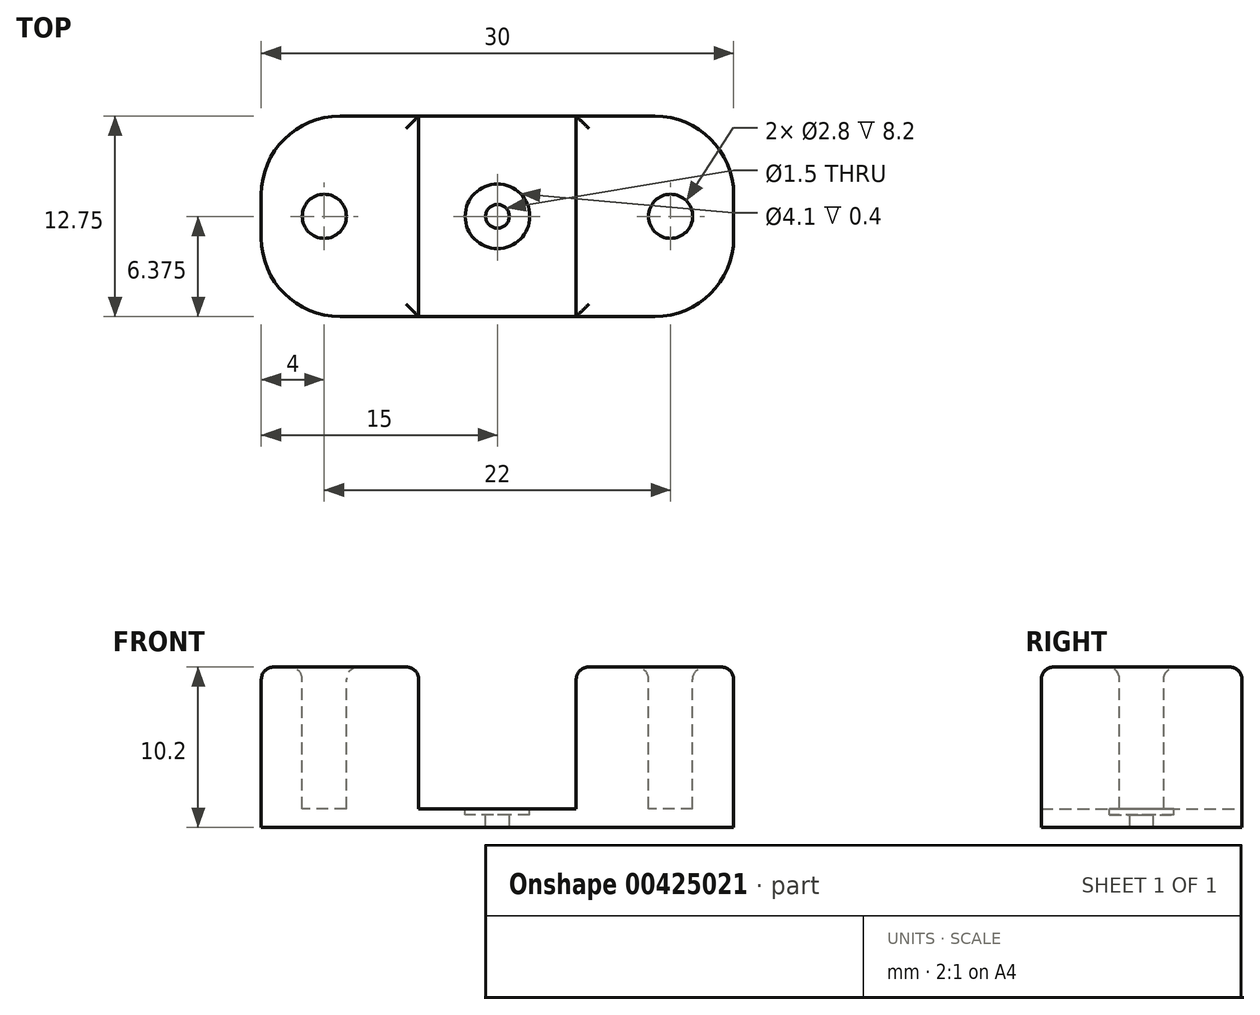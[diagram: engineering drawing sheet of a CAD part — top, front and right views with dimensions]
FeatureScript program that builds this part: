
annotation { "Feature Type Name" : "Feature", "Feature Type Description" : "" }
export const myFeature = defineFeature(function(context is Context, id is Id, definition is map)
    precondition{}
    {
        {
            var Q0;
            Q0=qCreatedBy(makeId("Front.planeOp"),FACE);
            var sketch = newSketch(context, id + "F0", { "sketchPlane" : qUnion([Q0])});
            skLineSegment(sketch, "E0", {"start": v(0, 0) * mm, "end": v(5, 0) * mm});
            skLineSegment(sketch, "E1", {"start": v(5, 0) * mm, "end": v(5, 9) * mm});
            skLineSegment(sketch, "E2", {"start": v(15, 9) * mm, "end": v(5, 9) * mm});
            skLineSegment(sketch, "E3", {"start": v(15, 9) * mm, "end": v(15, -1.2) * mm});
            skLineSegment(sketch, "E4", {"start": v(15, -1.2) * mm, "end": v(0, -1.2) * mm});
            skLineSegment(sketch, "E5.MirrorCS", {"start": v(0, 0) * mm, "end": v(-5, 0) * mm});
            skLineSegment(sketch, "E6.MirrorCS", {"start": v(-5, 0) * mm, "end": v(-5, 9) * mm});
            skLineSegment(sketch, "E7.MirrorCS", {"start": v(-15, 9) * mm, "end": v(-15, -1.2) * mm});
            skLineSegment(sketch, "E8.MirrorCS", {"start": v(-15, -1.2) * mm, "end": v(0, -1.2) * mm});
            skLineSegment(sketch, "E9.MirrorCS", {"start": v(-15, 9) * mm, "end": v(-5, 9) * mm});
            skSolve(sketch);
        }
        {
            var Q0;
            Q0 = qSketchRegion(id + "F0", true);
            extrude(context, id + "F1", {"entities" : qUnion([Q0]), "depth" : 12.75 * mm});
        }
        {
            var Q0;
            Q0=makeQuery(id+"F1.opExtrude","CAP_EDGE",EDGE,{"disambiguationData":[OSD([sQuery(id+"F0.wireOp",EDGE,"E3")])],"isStart":false});
            var Q1;
            Q1=makeQuery(id+"F1.opExtrude","CAP_EDGE",EDGE,{"disambiguationData":[OSD([sQuery(id+"F0.wireOp",EDGE,"E3")])],"isStart":true});
            var Q2;
            Q2=makeQuery(id+"F1.opExtrude","CAP_EDGE",EDGE,{"disambiguationData":[OSD([sQuery(id+"F0.wireOp",EDGE,"E7.MirrorCS")])],"isStart":false});
            var Q3;
            Q3=makeQuery(id+"F1.opExtrude","CAP_EDGE",EDGE,{"disambiguationData":[OSD([sQuery(id+"F0.wireOp",EDGE,"E7.MirrorCS")])],"isStart":true});
            fillet(context, id + "F2", {"entities" : qUnion([Q0, Q1, Q2, Q3]), "radius" : 5 * mm, "tangentPropagation" : true, "allowEdgeOverflow" : false});
        }
        {
            var Q0;
            Q0=makeQuery(id+"F1.opExtrude","SWEPT_FACE",FACE,{"disambiguationData":[OSD([sQuery(id+"F0.wireOp",EDGE,"E0"),sQuery(id+"F0.wireOp",EDGE,"E5.MirrorCS")])]});
            var sketch = newSketch(context, id + "F3", { "sketchPlane" : qUnion([Q0])});
            skCircle(sketch, "E10", {"center": v(0, -6.38) * mm, "radius": 0.75 * mm});
            skPoint(sketch, "E10.centerSnap0", {"position": v(0, -12.75) * mm});
            skCircle(sketch, "E11", {"center": v(0, -6.38) * mm, "radius": 2.05 * mm});
            skSolve(sketch);
        }
        {
            var Q0;
            Q0=makeQuery(id+"F3.imprint","IMPRINT",FACE,{"disambiguationData":[TD([[makeQuery(id+"F3.imprint","IMPRINT",EDGE,{"derivedFrom":sQuery(id+"F3.wireOp",EDGE,"E10")}),1.0]])]});
            extrude(context, id + "F4", {"entities" : qUnion([Q0]), "operationType" : NewBodyOperationType.REMOVE, "endBound" : BoundingType.THROUGH_ALL, "oppositeDirection" : true, "depth" : 25 * mm});
        }
        {
            var Q0;
            Q0=makeQuery(id+"F3.imprint","IMPRINT",FACE,{"disambiguationData":[TD([[makeQuery(id+"F3.imprint","IMPRINT",EDGE,{"derivedFrom":sQuery(id+"F3.wireOp",EDGE,"E10")}),-1.0]])]});
            extrude(context, id + "F5", {"entities" : qUnion([Q0]), "operationType" : NewBodyOperationType.REMOVE, "oppositeDirection" : true, "depth" : .4 * mm});
        }
        {
            var Q0;
            Q0=makeQuery(id+"F1.opExtrude","SWEPT_FACE",FACE,{"disambiguationData":[OSD([sQuery(id+"F0.wireOp",EDGE,"E2")])]});
            var sketch = newSketch(context, id + "F6", { "sketchPlane" : qUnion([Q0])});
            skCircle(sketch, "E12", {"center": v(11, -6.38) * mm, "radius": 1.4 * mm});
            skPoint(sketch, "E12.centerSnap0", {"position": v(5, -6.38) * mm});
            skCircle(sketch, "E13.MirrorC", {"center": v(-11, -6.38) * mm, "radius": 1.4 * mm});
            skSolve(sketch);
        }
        {
            var Q0;
            Q0 = qSketchRegion(id + "F6", true);
            extrude(context, id + "F7", {"entities" : qUnion([Q0]), "operationType" : NewBodyOperationType.REMOVE, "oppositeDirection" : true, "depth" : 9 * mm});
        }
        {
            var Q0;
            Q0=makeQuery(id+"F1.opExtrude","SWEPT_FACE",FACE,{"disambiguationData":[OSD([sQuery(id+"F0.wireOp",EDGE,"E9.MirrorCS")])]});
            var Q1;
            Q1=makeQuery(id+"F1.opExtrude","SWEPT_FACE",FACE,{"disambiguationData":[OSD([sQuery(id+"F0.wireOp",EDGE,"E2")])]});
            fillet(context, id + "F8", {"entities" : qUnion([Q0, Q1]), "radius" : .8 * mm, "tangentPropagation" : true, "allowEdgeOverflow" : false});
        }
    });
